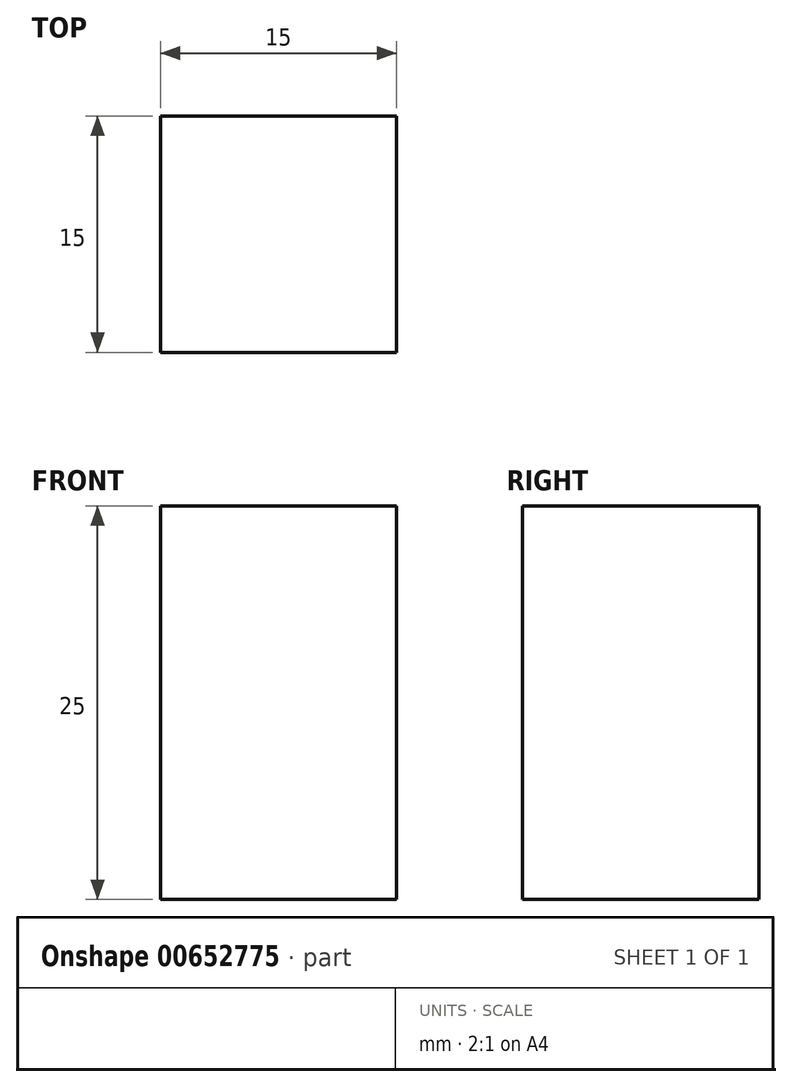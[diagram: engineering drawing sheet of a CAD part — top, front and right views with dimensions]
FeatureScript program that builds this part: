
annotation { "Feature Type Name" : "Feature", "Feature Type Description" : "" }
export const myFeature = defineFeature(function(context is Context, id is Id, definition is map)
    precondition{}
    {
        {
            var Q0;
            Q0=qCreatedBy(makeId("Top.planeOp"),FACE);
            var sketch = newSketch(context, id + "F0", { "sketchPlane" : qUnion([Q0])});
            skLineSegment(sketch, "E0.bottom", {"start": v(0, 0) * mm, "end": v(-15, 0) * mm});
            skLineSegment(sketch, "E0.top", {"start": v(0, 15) * mm, "end": v(-15, 15) * mm});
            skLineSegment(sketch, "E0.left", {"start": v(0, 0) * mm, "end": v(0, 15) * mm});
            skLineSegment(sketch, "E0.right", {"start": v(-15, 0) * mm, "end": v(-15, 15) * mm});
            skSolve(sketch);
        }
        {
            var Q0;
            Q0=makeQuery(id+"F0.imprint","IMPRINT",FACE,{"disambiguationData":[TD([[makeQuery(id+"F0.imprint","IMPRINT",EDGE,{"derivedFrom":sQuery(id+"F0.wireOp",EDGE,"E0.bottom")}),-1.0]])]});
            extrude(context, id + "F1", {"entities" : qUnion([Q0]), "depth" : 25 * mm, "offsetDistance" : 25 * mm});
        }
    });
